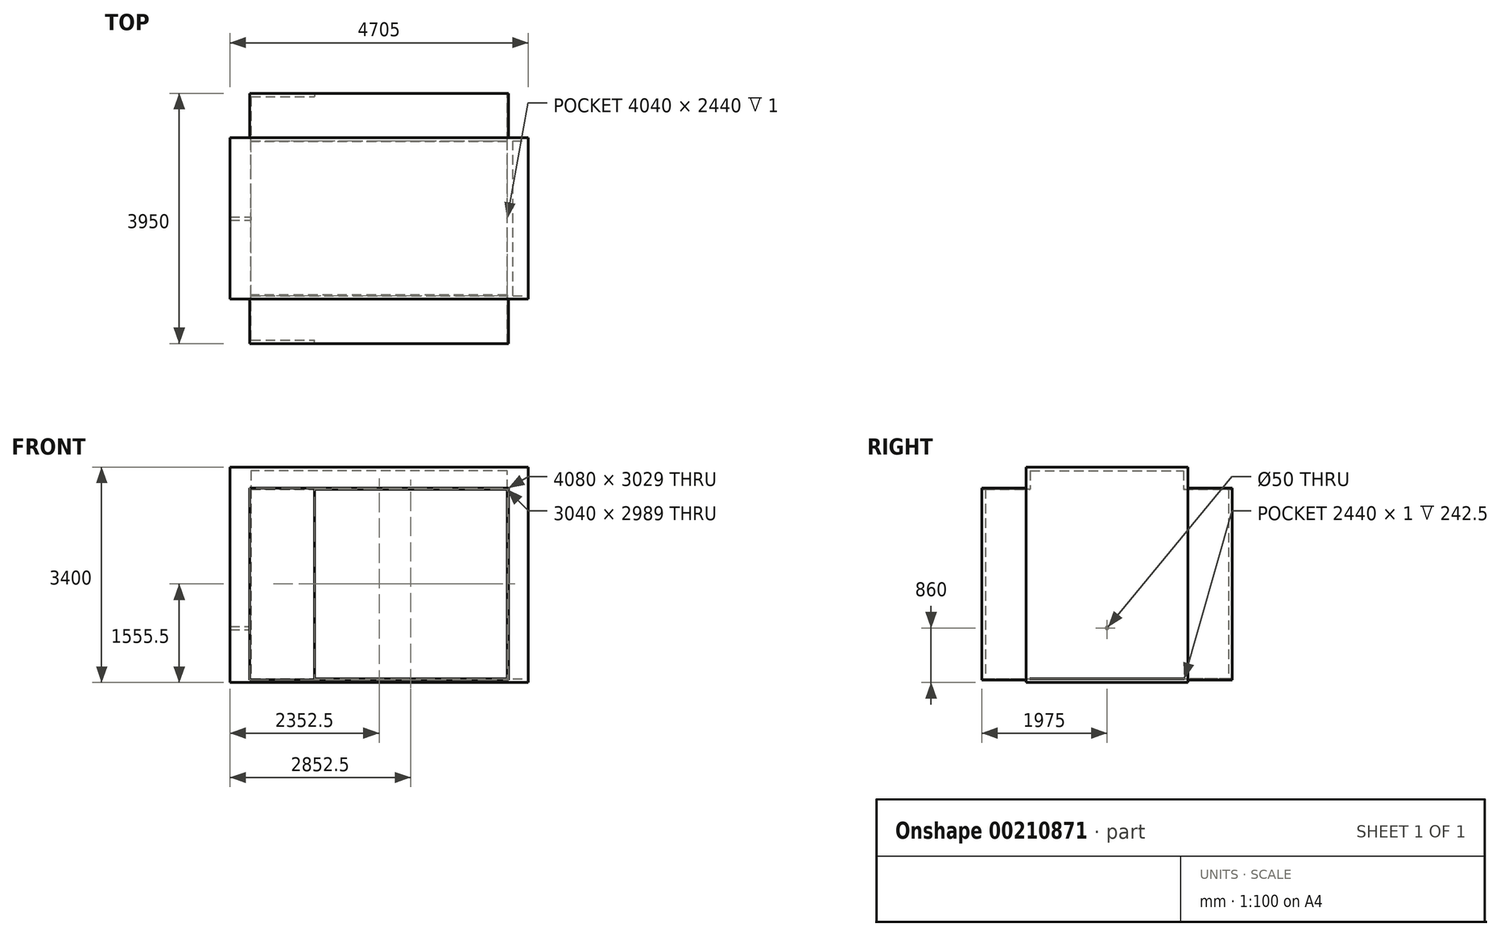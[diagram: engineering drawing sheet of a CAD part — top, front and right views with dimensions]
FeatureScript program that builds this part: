
annotation { "Feature Type Name" : "Feature", "Feature Type Description" : "" }
export const myFeature = defineFeature(function(context is Context, id is Id, definition is map)
    precondition{}
    {
        {
            var Q0;
            Q0=qCreatedBy(makeId("Front.planeOp"),FACE);
            var sketch = newSketch(context, id + "F0", { "sketchPlane" : qUnion([Q0])});
            skLineSegment(sketch, "E0.bottom", {"start": v(2352.5, -1700) * mm, "end": v(-2352.5, -1700) * mm});
            skLineSegment(sketch, "E0.top", {"start": v(2352.5, 1700) * mm, "end": v(-2352.5, 1700) * mm});
            skLineSegment(sketch, "E0.left", {"start": v(2352.5, -1700) * mm, "end": v(2352.5, 1700) * mm});
            skLineSegment(sketch, "E0.right", {"start": v(-2352.5, -1700) * mm, "end": v(-2352.5, 1700) * mm});
            skPoint(sketch, "E0.middle", {"position": v(0, 0) * mm});
            skLineSegment(sketch, "E1.bottom", {"start": v(2020, -1640) * mm, "end": v(-2020, -1640) * mm});
            skLineSegment(sketch, "E1.top", {"start": v(2020, 1640) * mm, "end": v(-2020, 1640) * mm});
            skLineSegment(sketch, "E1.left", {"start": v(2020, -1640) * mm, "end": v(2020, 1640) * mm});
            skLineSegment(sketch, "E1.right", {"start": v(-2020, -1640) * mm, "end": v(-2020, 1640) * mm});
            skSolve(sketch);
        }
        {
            var Q0;
            Q0=qSketchRegion(id+"F0",true);
            extrude(context, id + "F1", {"entities" : qUnion([Q0]), "depth" : 2550 * mm});
        }
        {
            var Q0;
            Q0=makeQuery(id+"F1.opExtrude","SWEPT_FACE",FACE,{"disambiguationData":[OSD([sQuery(id+"F0.wireOp",EDGE,"E1.right")])]});
            var sketch = newSketch(context, id + "F2", { "sketchPlane" : qUnion([Q0])});
            skLineSegment(sketch, "E2.bottom", {"start": v(-2550, 1640) * mm, "end": v(-2485, 1640) * mm});
            skLineSegment(sketch, "E2.top", {"start": v(-2550, 1350) * mm, "end": v(-2485, 1350) * mm});
            skLineSegment(sketch, "E2.left", {"start": v(-2550, 1640) * mm, "end": v(-2550, 1350) * mm});
            skLineSegment(sketch, "E2.right", {"start": v(-2485, 1640) * mm, "end": v(-2485, 1350) * mm});
            skLineSegment(sketch, "E3", {"start": v(-1275, -1640) * mm, "end": v(-1275, 507.53) * mm, "construction": true});
            skLineSegment(sketch, "E4.MirrorCS", {"start": v(0, 1640) * mm, "end": v(0, 1350) * mm});
            skLineSegment(sketch, "E5.MirrorCS", {"start": v(-65, 1640) * mm, "end": v(-65, 1350) * mm});
            skLineSegment(sketch, "E6.MirrorCS", {"start": v(0, 1350) * mm, "end": v(-65, 1350) * mm});
            skLineSegment(sketch, "E7.MirrorCS", {"start": v(0, 1640) * mm, "end": v(-65, 1640) * mm});
            skSolve(sketch);
        }
        {
            var Q0;
            Q0=qSketchRegion(id+"F2",true);
            extrude(context, id + "F3", {"entities" : qUnion([Q0]), "operationType" : NewBodyOperationType.ADD, "endBound" : BoundingType.UP_TO_NEXT, "depth" : 25 * mm});
        }
        {
            var Q0;
            Q0=makeQuery(id+"F1.opExtrude","SWEPT_FACE",FACE,{"disambiguationData":[OSD([sQuery(id+"F0.wireOp",EDGE,"E1.right")])]});
            var sketch = newSketch(context, id + "F4", { "sketchPlane" : qUnion([Q0])});
            skLineSegment(sketch, "E8", {"start": v(-1275, -1640) * mm, "end": v(-1275, 1640) * mm, "construction": true});
            skCircle(sketch, "E9", {"center": v(-1275, -840) * mm, "radius": 25 * mm});
            skSolve(sketch);
        }
        {
            var Q0;
            Q0=qSketchRegion(id+"F4",true);
            extrude(context, id + "F5", {"entities" : qUnion([Q0]), "operationType" : NewBodyOperationType.REMOVE, "endBound" : BoundingType.THROUGH_ALL, "oppositeDirection" : true, "depth" : 25 * mm});
        }
        {
            var Q0;
            Q0=makeQuery(id+"FKxTItzzNBGIn2z_1.boolean.opBoolean","MERGE",FACE,{"derivedFrom":[makeQuery(id+"F1.opExtrude","SWEPT_FACE",FACE,{"disambiguationData":[OSD([sQuery(id+"F0.wireOp",EDGE,"E1.bottom")])]}),makeQuery(id+"FKxTItzzNBGIn2z_1.opExtrude","SWEPT_FACE",FACE,{"disambiguationData":[OSD([sQuery(id+"FqS4iGN8Oapy3Km_1.wireOp",EDGE,"61F1EtYj-JJJJ-jnj6-z9AF-rj3ERCSz4D68.top")])]})]});
            var sketch = newSketch(context, id + "F6", { "sketchPlane" : qUnion([Q0])});
            skLineSegment(sketch, "E10.bottom", {"start": v(2110, -2495) * mm, "end": v(2352.5, -2495) * mm});
            skLineSegment(sketch, "E10.top", {"start": v(2110, -55) * mm, "end": v(2352.5, -55) * mm});
            skLineSegment(sketch, "E10.left", {"start": v(2110, -2495) * mm, "end": v(2110, -55) * mm});
            skLineSegment(sketch, "E10.right", {"start": v(2352.5, -2495) * mm, "end": v(2352.5, -55) * mm});
            skSolve(sketch);
        }
        {
            var Q0;
            Q0=qSketchRegion(id+"F6",true);
            extrude(context, id + "F7", {"entities" : qUnion([Q0]), "operationType" : NewBodyOperationType.REMOVE, "oppositeDirection" : true, "depth" : 1 * mm});
        }
        {
            var Q0;
            Q0=makeQuery(id+"F3.boolean.opBoolean","MERGE",FACE,{"derivedFrom":[makeQuery(id+"F1.opExtrude","CAP_FACE",FACE,{"disambiguationData":[OSD([sQuery(id+"F0.wireOp",EDGE,"E0.bottom"),sQuery(id+"F0.wireOp",EDGE,"E0.top"),sQuery(id+"F0.wireOp",EDGE,"E0.left"),sQuery(id+"F0.wireOp",EDGE,"E0.right"),sQuery(id+"F0.wireOp",EDGE,"E1.bottom"),sQuery(id+"F0.wireOp",EDGE,"E1.top"),sQuery(id+"F0.wireOp",EDGE,"E1.left"),sQuery(id+"F0.wireOp",EDGE,"E1.right")])],"isStart":false}),makeQuery(id+"F3.opExtrude","SWEPT_FACE",FACE,{"disambiguationData":[OSD([sQuery(id+"F2.wireOp",EDGE,"E2.left")])]})]});
            var sketch = newSketch(context, id + "F8", { "sketchPlane" : qUnion([Q0])});
            skLineSegment(sketch, "E11.bottom", {"start": v(-2020, 1350) * mm, "end": v(2020, 1350) * mm});
            skLineSegment(sketch, "E11.top", {"start": v(-2020, -1639) * mm, "end": v(2020, -1639) * mm});
            skLineSegment(sketch, "E11.left", {"start": v(-2020, 1350) * mm, "end": v(-2020, -1639) * mm});
            skLineSegment(sketch, "E11.right", {"start": v(2020, 1350) * mm, "end": v(2020, -1639) * mm});
            skLineSegment(sketch, "E12.bottom", {"start": v(-2040, 1370) * mm, "end": v(2040, 1370) * mm});
            skLineSegment(sketch, "E12.top", {"start": v(-2040, -1659) * mm, "end": v(2040, -1659) * mm});
            skLineSegment(sketch, "E12.left", {"start": v(-2040, 1370) * mm, "end": v(-2040, -1659) * mm});
            skLineSegment(sketch, "E12.right", {"start": v(2040, 1370) * mm, "end": v(2040, -1659) * mm});
            skSolve(sketch);
        }
        {
            var Q0;
            Q0 = qSketchRegion(id + "F8", true);
            extrude(context, id + "F9", {"entities" : qUnion([Q0]), "operationType" : NewBodyOperationType.ADD, "depth" : 700 * mm});
        }
        {
            var Q0;
            Q0=makeQuery(id+"F3.boolean.opBoolean","MERGE",FACE,{"derivedFrom":[makeQuery(id+"F1.opExtrude","CAP_FACE",FACE,{"disambiguationData":[OSD([sQuery(id+"F0.wireOp",EDGE,"E0.bottom"),sQuery(id+"F0.wireOp",EDGE,"E0.top"),sQuery(id+"F0.wireOp",EDGE,"E0.left"),sQuery(id+"F0.wireOp",EDGE,"E0.right"),sQuery(id+"F0.wireOp",EDGE,"E1.bottom"),sQuery(id+"F0.wireOp",EDGE,"E1.top"),sQuery(id+"F0.wireOp",EDGE,"E1.left"),sQuery(id+"F0.wireOp",EDGE,"E1.right")])],"isStart":true}),makeQuery(id+"F3.opExtrude","SWEPT_FACE",FACE,{"disambiguationData":[OSD([sQuery(id+"F2.wireOp",EDGE,"E4.MirrorCS")])]})]});
            var sketch = newSketch(context, id + "F10", { "sketchPlane" : qUnion([Q0])});
            skLineSegment(sketch, "E13.bottom", {"start": v(-2020, 1350) * mm, "end": v(2020, 1350) * mm});
            skLineSegment(sketch, "E13.top", {"start": v(-2020, -1639) * mm, "end": v(2020, -1639) * mm});
            skLineSegment(sketch, "E13.left", {"start": v(-2020, 1350) * mm, "end": v(-2020, -1639) * mm});
            skLineSegment(sketch, "E13.right", {"start": v(2020, 1350) * mm, "end": v(2020, -1639) * mm});
            skLineSegment(sketch, "E14.bottom", {"start": v(-2040, 1370) * mm, "end": v(2040, 1370) * mm});
            skLineSegment(sketch, "E14.top", {"start": v(-2040, -1659) * mm, "end": v(2040, -1659) * mm});
            skLineSegment(sketch, "E14.left", {"start": v(-2040, 1370) * mm, "end": v(-2040, -1659) * mm});
            skLineSegment(sketch, "E14.right", {"start": v(2040, 1370) * mm, "end": v(2040, -1659) * mm});
            skSolve(sketch);
        }
        {
            var Q0;
            Q0 = qSketchRegion(id + "F10", true);
            extrude(context, id + "F11", {"entities" : qUnion([Q0]), "operationType" : NewBodyOperationType.ADD, "depth" : 700 * mm});
        }
        {
            var Q0;
            Q0=makeQuery(id+"F11.opExtrude","SWEPT_FACE",FACE,{"disambiguationData":[OSD([sQuery(id+"F10.wireOp",EDGE,"E13.top")])]});
            var sketch = newSketch(context, id + "F12", { "sketchPlane" : qUnion([Q0])});
            skLineSegment(sketch, "E15.bottom", {"start": v(-2020, 700) * mm, "end": v(-1020, 700) * mm});
            skLineSegment(sketch, "E15.top", {"start": v(-2020, 645) * mm, "end": v(-1020, 645) * mm});
            skLineSegment(sketch, "E15.left", {"start": v(-2020, 700) * mm, "end": v(-2020, 645) * mm});
            skLineSegment(sketch, "E15.right", {"start": v(-1020, 700) * mm, "end": v(-1020, 645) * mm});
            skSolve(sketch);
        }
        {
            var Q0;
            Q0 = qSketchRegion(id + "F12", true);
            var Q1;
            Q1=makeQuery(id+"F11.boolean.opBoolean","MERGE",FACE,{"derivedFrom":[makeQuery(id+"F3.opExtrude","SWEPT_FACE",FACE,{"disambiguationData":[OSD([sQuery(id+"F2.wireOp",EDGE,"E6.MirrorCS")])]}),makeQuery(id+"F11.opExtrude","SWEPT_FACE",FACE,{"disambiguationData":[OSD([sQuery(id+"F10.wireOp",EDGE,"E13.bottom")])]})]});
            extrude(context, id + "F13", {"entities" : qUnion([Q0]), "operationType" : NewBodyOperationType.ADD, "endBound" : BoundingType.UP_TO_SURFACE, "endBoundEntityFace" : qUnion([Q1]), "depth" : 25 * mm});
        }
        {
            var Q0;
            Q0=makeQuery(id+"F9.opExtrude","SWEPT_FACE",FACE,{"disambiguationData":[OSD([sQuery(id+"F8.wireOp",EDGE,"E11.top")])]});
            var sketch = newSketch(context, id + "F14", { "sketchPlane" : qUnion([Q0])});
            skLineSegment(sketch, "E16.bottom", {"start": v(-2020, -3250) * mm, "end": v(-1020, -3250) * mm});
            skLineSegment(sketch, "E16.top", {"start": v(-2020, -3195) * mm, "end": v(-1020, -3195) * mm});
            skLineSegment(sketch, "E16.left", {"start": v(-2020, -3250) * mm, "end": v(-2020, -3195) * mm});
            skLineSegment(sketch, "E16.right", {"start": v(-1020, -3250) * mm, "end": v(-1020, -3195) * mm});
            skSolve(sketch);
        }
        {
            var Q0;
            Q0 = qSketchRegion(id + "F14", true);
            extrude(context, id + "F15", {"entities" : qUnion([Q0]), "operationType" : NewBodyOperationType.ADD, "endBound" : BoundingType.UP_TO_NEXT, "depth" : 25 * mm});
        }
        {
            var Q0;
            Q0=makeQuery(id+"F1.opExtrude","SWEPT_FACE",FACE,{"disambiguationData":[OSD([sQuery(id+"F0.wireOp",EDGE,"E1.bottom")])]});
            var sketch = newSketch(context, id + "F16", { "sketchPlane" : qUnion([Q0])});
            skLineSegment(sketch, "E17", {"start": v(-2020, -1275) * mm, "end": v(0, -1275) * mm, "construction": true});
            skLineSegment(sketch, "E18.bottom", {"start": v(-2020, -55) * mm, "end": v(2020, -55) * mm});
            skLineSegment(sketch, "E18.top", {"start": v(-2020, -2495) * mm, "end": v(2020, -2495) * mm});
            skLineSegment(sketch, "E18.left", {"start": v(-2020, -55) * mm, "end": v(-2020, -2495) * mm});
            skLineSegment(sketch, "E18.right", {"start": v(2020, -55) * mm, "end": v(2020, -2495) * mm});
            skPoint(sketch, "E18.middle", {"position": v(0, -1275) * mm});
            skSolve(sketch);
        }
        {
            var Q0;
            Q0 = qSketchRegion(id + "F16", true);
            extrude(context, id + "F17", {"entities" : qUnion([Q0]), "operationType" : NewBodyOperationType.REMOVE, "oppositeDirection" : true, "depth" : 1 * mm});
        }
    });
